FCSTD DOCUMENT  (FreeCAD 0.18R13588 (Git))
Label: footprint-Edge-template
License: All rights reserved
LicenseURL: http://en.wikipedia.org/wiki/All_rights_reserved
objects: Sketcher::SketchObject×4, App::Annotation×2, App::DocumentObjectGroup×1
note: 4 computed .brp shape members not serialized (recipe doc carries the construction recipe); baked Part::Feature solids carry a one-line shape summary decoded from their .brp

FEATURE [Sketcher::SketchObject] Sketch004  label="F_Fab_0.1"
  sketch-geometry (4):
    g0: Circle CenterX=0.0195 CenterY=-0.011 CenterZ=0 NormalX=0 NormalY=0 NormalZ=1 AngleXU=0 Radius=3.1
    g1: Circle CenterX=0.0195 CenterY=-49.011 CenterZ=0 NormalX=0 NormalY=0 NormalZ=1 AngleXU=0 Radius=3.1
    g2: Circle CenterX=58.0195 CenterY=-0.011 CenterZ=0 NormalX=0 NormalY=0 NormalZ=1 AngleXU=0 Radius=3.1
    g3: Circle CenterX=58.0195 CenterY=-49.011 CenterZ=0 NormalX=0 NormalY=0 NormalZ=1 AngleXU=0 Radius=3.1
  constraints (4):
    c: Radius(g0) = 3.1
    c: Radius(g2) = 3.1
    c: Radius(g3) = 3.1
    c: Radius(g1) = 3.1
FEATURE [Sketcher::SketchObject] Sketch  label="Edge_Cuts_0.15"
  sketch-geometry (20):
    g0: LineSegment StartX=-0.4805 StartY=3.739 StartZ=0 EndX=58.5195 EndY=3.739 EndZ=0
    g1: ArcOfCircle CenterX=-0.4805 CenterY=0.739 CenterZ=0 NormalX=0 NormalY=0 NormalZ=1 AngleXU=1.5708 Radius=3 StartAngle=0 EndAngle=1.5708
    g2: ArcOfCircle CenterX=58.5195 CenterY=0.739 CenterZ=0 NormalX=0 NormalY=0 NormalZ=1 AngleXU=0 Radius=3 StartAngle=0 EndAngle=1.5708
    g3: LineSegment StartX=-3.4805 StartY=0.739 StartZ=0 EndX=-3.4805 EndY=-15.261 EndZ=0
    g4: LineSegment StartX=61.5195 StartY=0.739 StartZ=0 EndX=61.5195 EndY=-49.761 EndZ=0
    g5: ArcOfCircle CenterX=-2.4805 CenterY=-15.261 CenterZ=0 NormalX=0 NormalY=0 NormalZ=1 AngleXU=-3.14159 Radius=1 StartAngle=0 EndAngle=1.5708
    g6: ArcOfCircle CenterX=58.5195 CenterY=-49.761 CenterZ=0 NormalX=0 NormalY=0 NormalZ=1 AngleXU=-1.5708 Radius=3 StartAngle=0 EndAngle=1.5708
    g7: LineSegment StartX=-2.4805 StartY=-16.261 StartZ=0 EndX=0.5195 EndY=-16.261 EndZ=0
    g8: LineSegment StartX=-0.4805 StartY=-52.761 StartZ=0 EndX=58.5195 EndY=-52.761 EndZ=0
    g9: ArcOfCircle CenterX=0.5195 CenterY=-17.261 CenterZ=0 NormalX=0 NormalY=0 NormalZ=1 AngleXU=0 Radius=1 StartAngle=0 EndAngle=1.5708
    g10: ArcOfCircle CenterX=-0.4805 CenterY=-49.761 CenterZ=0 NormalX=0 NormalY=0 NormalZ=1 AngleXU=3.14159 Radius=3 StartAngle=0 EndAngle=1.5708
    g11: LineSegment StartX=1.5195 StartY=-17.261 StartZ=0 EndX=1.5195 EndY=-32.261 EndZ=0
    g12: LineSegment StartX=-3.4805 StartY=-34.261 StartZ=0 EndX=-3.4805 EndY=-49.761 EndZ=0
    g13: ArcOfCircle CenterX=0.5195 CenterY=-32.261 CenterZ=0 NormalX=0 NormalY=0 NormalZ=1 AngleXU=-1.5708 Radius=1 StartAngle=0 EndAngle=1.5708
    g14: ArcOfCircle CenterX=-2.4805 CenterY=-34.261 CenterZ=0 NormalX=0 NormalY=0 NormalZ=1 AngleXU=1.5708 Radius=1 StartAngle=0 EndAngle=1.5708
    g15: LineSegment StartX=-2.4805 StartY=-33.261 StartZ=0 EndX=0.5195 EndY=-33.261 EndZ=0
    g16: LineSegment StartX=42.5195 StartY=-33.761 StartZ=0 EndX=42.5195 EndY=-48.761 EndZ=0
    g17: ArcOfCircle CenterX=41.5195 CenterY=-33.761 CenterZ=0 NormalX=0 NormalY=0 NormalZ=1 AngleXU=0 Radius=1 StartAngle=0 EndAngle=3.14159
    g18: ArcOfCircle CenterX=41.5195 CenterY=-48.761 CenterZ=0 NormalX=0 NormalY=0 NormalZ=1 AngleXU=3.14159 Radius=1 StartAngle=0 EndAngle=3.14159
    g19: LineSegment StartX=40.5195 StartY=-33.761 StartZ=0 EndX=40.5195 EndY=-48.761 EndZ=0
FEATURE [App::Annotation] Text  label="Ref#_1.0mm"
  LabelText = REF**
  Position = (1,-7,0)
FEATURE [App::Annotation] Text001  label="Value#_1.0mm"
  LabelText = Value 
  Position = (1,-10,0)
FEATURE [Sketcher::SketchObject] Sketch006  label="Pads_TH_SMD"
  sketch-geometry (83):
    g0: LineSegment StartX=4 StartY=-0.411 StartZ=0 EndX=5.76617 EndY=-0.411 EndZ=0
    g1: LineSegment StartX=5.76617 StartY=-0.411 StartZ=0 EndX=5.76617 EndY=-2.151 EndZ=0
    g2: LineSegment StartX=5.76617 StartY=-2.151 StartZ=0 EndX=4 EndY=-2.151 EndZ=0
    g3: LineSegment StartX=4 StartY=-2.151 StartZ=0 EndX=4 EndY=-0.411 EndZ=0
    g4: Circle CenterX=4.889 CenterY=1.259 CenterZ=0 NormalX=0 NormalY=0 NormalZ=1 AngleXU=0 Radius=0.87
    g5: Circle CenterX=7.429 CenterY=-1.281 CenterZ=0 NormalX=0 NormalY=0 NormalZ=1 AngleXU=0 Radius=0.87
    g6: Circle CenterX=7.429 CenterY=1.259 CenterZ=0 NormalX=0 NormalY=0 NormalZ=1 AngleXU=0 Radius=0.87
    g7: Circle CenterX=9.969 CenterY=-1.281 CenterZ=0 NormalX=0 NormalY=0 NormalZ=1 AngleXU=0 Radius=0.87
    g8: Circle CenterX=9.969 CenterY=1.259 CenterZ=0 NormalX=0 NormalY=0 NormalZ=1 AngleXU=0 Radius=0.87
    g9: Circle CenterX=12.509 CenterY=-1.281 CenterZ=0 NormalX=0 NormalY=0 NormalZ=1 AngleXU=0 Radius=0.87
    g10: Circle CenterX=12.509 CenterY=1.259 CenterZ=0 NormalX=0 NormalY=0 NormalZ=1 AngleXU=0 Radius=0.87
    g11: Circle CenterX=15.049 CenterY=-1.281 CenterZ=0 NormalX=0 NormalY=0 NormalZ=1 AngleXU=0 Radius=0.87
    g12: Circle CenterX=15.049 CenterY=1.259 CenterZ=0 NormalX=0 NormalY=0 NormalZ=1 AngleXU=0 Radius=0.87
    g13: Circle CenterX=17.589 CenterY=-1.281 CenterZ=0 NormalX=0 NormalY=0 NormalZ=1 AngleXU=0 Radius=0.87
    g14: Circle CenterX=17.589 CenterY=1.259 CenterZ=0 NormalX=0 NormalY=0 NormalZ=1 AngleXU=0 Radius=0.87
    g15: Circle CenterX=20.129 CenterY=-1.281 CenterZ=0 NormalX=0 NormalY=0 NormalZ=1 AngleXU=0 Radius=0.87
    g16: Circle CenterX=20.129 CenterY=1.259 CenterZ=0 NormalX=0 NormalY=0 NormalZ=1 AngleXU=0 Radius=0.87
    g17: Circle CenterX=22.669 CenterY=-1.281 CenterZ=0 NormalX=0 NormalY=0 NormalZ=1 AngleXU=0 Radius=0.87
    g18: Circle CenterX=22.669 CenterY=1.259 CenterZ=0 NormalX=0 NormalY=0 NormalZ=1 AngleXU=0 Radius=0.87
    g19: Circle CenterX=25.209 CenterY=-1.281 CenterZ=0 NormalX=0 NormalY=0 NormalZ=1 AngleXU=0 Radius=0.87
    g20: Circle CenterX=25.209 CenterY=1.259 CenterZ=0 NormalX=0 NormalY=0 NormalZ=1 AngleXU=0 Radius=0.87
    g21: Circle CenterX=27.749 CenterY=-1.281 CenterZ=0 NormalX=0 NormalY=0 NormalZ=1 AngleXU=0 Radius=0.87
    g22: Circle CenterX=27.749 CenterY=1.259 CenterZ=0 NormalX=0 NormalY=0 NormalZ=1 AngleXU=0 Radius=0.87
    g23: Circle CenterX=30.289 CenterY=-1.281 CenterZ=0 NormalX=0 NormalY=0 NormalZ=1 AngleXU=0 Radius=0.87
    g24: Circle CenterX=30.289 CenterY=1.259 CenterZ=0 NormalX=0 NormalY=0 NormalZ=1 AngleXU=0 Radius=0.87
    g25: Circle CenterX=32.829 CenterY=-1.281 CenterZ=0 NormalX=0 NormalY=0 NormalZ=1 AngleXU=0 Radius=0.87
    g26: Circle CenterX=32.829 CenterY=1.259 CenterZ=0 NormalX=0 NormalY=0 NormalZ=1 AngleXU=0 Radius=0.87
    g27: Circle CenterX=35.369 CenterY=-1.281 CenterZ=0 NormalX=0 NormalY=0 NormalZ=1 AngleXU=0 Radius=0.87
    g28: Circle CenterX=35.369 CenterY=1.259 CenterZ=0 NormalX=0 NormalY=0 NormalZ=1 AngleXU=0 Radius=0.87
    g29: Circle CenterX=37.909 CenterY=-1.281 CenterZ=0 NormalX=0 NormalY=0 NormalZ=1 AngleXU=0 Radius=0.87
    g30: Circle CenterX=37.909 CenterY=1.259 CenterZ=0 NormalX=0 NormalY=0 NormalZ=1 AngleXU=0 Radius=0.87
    g31: Circle CenterX=40.449 CenterY=-1.281 CenterZ=0 NormalX=0 NormalY=0 NormalZ=1 AngleXU=0 Radius=0.87
    g32: Circle CenterX=40.449 CenterY=1.259 CenterZ=0 NormalX=0 NormalY=0 NormalZ=1 AngleXU=0 Radius=0.87
    g33: Circle CenterX=42.989 CenterY=-1.281 CenterZ=0 NormalX=0 NormalY=0 NormalZ=1 AngleXU=0 Radius=0.87
    g34: Circle CenterX=42.989 CenterY=1.259 CenterZ=0 NormalX=0 NormalY=0 NormalZ=1 AngleXU=0 Radius=0.87
    g35: Circle CenterX=45.529 CenterY=-1.281 CenterZ=0 NormalX=0 NormalY=0 NormalZ=1 AngleXU=0 Radius=0.87
    g36: Circle CenterX=45.529 CenterY=1.259 CenterZ=0 NormalX=0 NormalY=0 NormalZ=1 AngleXU=0 Radius=0.87
    g37: Circle CenterX=48.069 CenterY=-1.281 CenterZ=0 NormalX=0 NormalY=0 NormalZ=1 AngleXU=0 Radius=0.87
    g38: Circle CenterX=48.069 CenterY=1.259 CenterZ=0 NormalX=0 NormalY=0 NormalZ=1 AngleXU=0 Radius=0.87
    g39: Circle CenterX=50.609 CenterY=-1.281 CenterZ=0 NormalX=0 NormalY=0 NormalZ=1 AngleXU=0 Radius=0.87
    g40: Circle CenterX=50.609 CenterY=1.259 CenterZ=0 NormalX=0 NormalY=0 NormalZ=1 AngleXU=0 Radius=0.87
    g41: Circle CenterX=53.149 CenterY=-1.281 CenterZ=0 NormalX=0 NormalY=0 NormalZ=1 AngleXU=0 Radius=0.87
    g42: Circle CenterX=53.149 CenterY=1.259 CenterZ=0 NormalX=0 NormalY=0 NormalZ=1 AngleXU=0 Radius=0.87
    g43: Circle CenterX=22.6695 CenterY=-1.281 CenterZ=0 NormalX=0 NormalY=0 NormalZ=1 AngleXU=0 Radius=0.508
    g44: Circle CenterX=25.2095 CenterY=-1.281 CenterZ=0 NormalX=0 NormalY=0 NormalZ=1 AngleXU=0 Radius=0.508
    g45: Circle CenterX=25.2095 CenterY=1.259 CenterZ=0 NormalX=0 NormalY=0 NormalZ=1 AngleXU=0 Radius=0.508
    g46: Circle CenterX=22.6695 CenterY=1.259 CenterZ=0 NormalX=0 NormalY=0 NormalZ=1 AngleXU=0 Radius=0.508
    g47: Circle CenterX=20.1295 CenterY=1.259 CenterZ=0 NormalX=0 NormalY=0 NormalZ=1 AngleXU=0 Radius=0.508
    g48: Circle CenterX=20.1295 CenterY=-1.281 CenterZ=0 NormalX=0 NormalY=0 NormalZ=1 AngleXU=0 Radius=0.508
    g49: Circle CenterX=9.9695 CenterY=-1.281 CenterZ=0 NormalX=0 NormalY=0 NormalZ=1 AngleXU=0 Radius=0.508
    g50: Circle CenterX=12.5095 CenterY=-1.281 CenterZ=0 NormalX=0 NormalY=0 NormalZ=1 AngleXU=0 Radius=0.508
    g51: Circle CenterX=9.9695 CenterY=1.259 CenterZ=0 NormalX=0 NormalY=0 NormalZ=1 AngleXU=0 Radius=0.508
    g52: Circle CenterX=15.0495 CenterY=1.259 CenterZ=0 NormalX=0 NormalY=0 NormalZ=1 AngleXU=0 Radius=0.508
    g53: Circle CenterX=12.5095 CenterY=1.259 CenterZ=0 NormalX=0 NormalY=0 NormalZ=1 AngleXU=0 Radius=0.508
    g54: Circle CenterX=15.0495 CenterY=-1.281 CenterZ=0 NormalX=0 NormalY=0 NormalZ=1 AngleXU=0 Radius=0.508
    g55: Circle CenterX=17.5895 CenterY=-1.281 CenterZ=0 NormalX=0 NormalY=0 NormalZ=1 AngleXU=0 Radius=0.508
    g56: Circle CenterX=17.5895 CenterY=1.259 CenterZ=0 NormalX=0 NormalY=0 NormalZ=1 AngleXU=0 Radius=0.508
    g57: Circle CenterX=7.4295 CenterY=-1.281 CenterZ=0 NormalX=0 NormalY=0 NormalZ=1 AngleXU=0 Radius=0.508
    g58: Circle CenterX=7.4295 CenterY=1.259 CenterZ=0 NormalX=0 NormalY=0 NormalZ=1 AngleXU=0 Radius=0.508
    g59: Circle CenterX=4.8895 CenterY=-1.281 CenterZ=0 NormalX=0 NormalY=0 NormalZ=1 AngleXU=0 Radius=0.508
    g60: Circle CenterX=4.8895 CenterY=1.259 CenterZ=0 NormalX=0 NormalY=0 NormalZ=1 AngleXU=0 Radius=0.508
    g61: Circle CenterX=53.1495 CenterY=-1.281 CenterZ=0 NormalX=0 NormalY=0 NormalZ=1 AngleXU=0 Radius=0.508
    g62: Circle CenterX=48.0695 CenterY=-1.281 CenterZ=0 NormalX=0 NormalY=0 NormalZ=1 AngleXU=0 Radius=0.508
    g63: Circle CenterX=50.6095 CenterY=-1.281 CenterZ=0 NormalX=0 NormalY=0 NormalZ=1 AngleXU=0 Radius=0.508
    g64: Circle CenterX=40.4495 CenterY=-1.281 CenterZ=0 NormalX=0 NormalY=0 NormalZ=1 AngleXU=0 Radius=0.508
    g65: Circle CenterX=42.9895 CenterY=-1.281 CenterZ=0 NormalX=0 NormalY=0 NormalZ=1 AngleXU=0 Radius=0.508
    g66: Circle CenterX=45.5295 CenterY=-1.281 CenterZ=0 NormalX=0 NormalY=0 NormalZ=1 AngleXU=0 Radius=0.508
    g67: Circle CenterX=53.1495 CenterY=1.259 CenterZ=0 NormalX=0 NormalY=0 NormalZ=1 AngleXU=0 Radius=0.508
    g68: Circle CenterX=50.6095 CenterY=1.259 CenterZ=0 NormalX=0 NormalY=0 NormalZ=1 AngleXU=0 Radius=0.508
    g69: Circle CenterX=48.0695 CenterY=1.259 CenterZ=0 NormalX=0 NormalY=0 NormalZ=1 AngleXU=0 Radius=0.508
    g70: Circle CenterX=42.9895 CenterY=1.259 CenterZ=0 NormalX=0 NormalY=0 NormalZ=1 AngleXU=0 Radius=0.508
    g71: Circle CenterX=45.5295 CenterY=1.259 CenterZ=0 NormalX=0 NormalY=0 NormalZ=1 AngleXU=0 Radius=0.508
    g72: Circle CenterX=40.4495 CenterY=1.259 CenterZ=0 NormalX=0 NormalY=0 NormalZ=1 AngleXU=0 Radius=0.508
    g73: Circle CenterX=27.7495 CenterY=1.259 CenterZ=0 NormalX=0 NormalY=0 NormalZ=1 AngleXU=0 Radius=0.508
    g74: Circle CenterX=30.2895 CenterY=1.259 CenterZ=0 NormalX=0 NormalY=0 NormalZ=1 AngleXU=0 Radius=0.508
    g75: Circle CenterX=35.3695 CenterY=1.259 CenterZ=0 NormalX=0 NormalY=0 NormalZ=1 AngleXU=0 Radius=0.508
    g76: Circle CenterX=32.8295 CenterY=1.259 CenterZ=0 NormalX=0 NormalY=0 NormalZ=1 AngleXU=0 Radius=0.508
    g77: Circle CenterX=27.7495 CenterY=-1.281 CenterZ=0 NormalX=0 NormalY=0 NormalZ=1 AngleXU=0 Radius=0.508
    g78: Circle CenterX=30.2895 CenterY=-1.281 CenterZ=0 NormalX=0 NormalY=0 NormalZ=1 AngleXU=0 Radius=0.508
    g79: Circle CenterX=32.8295 CenterY=-1.281 CenterZ=0 NormalX=0 NormalY=0 NormalZ=1 AngleXU=0 Radius=0.508
    g80: Circle CenterX=35.3695 CenterY=-1.281 CenterZ=0 NormalX=0 NormalY=0 NormalZ=1 AngleXU=0 Radius=0.508
    g81: Circle CenterX=37.9095 CenterY=-1.281 CenterZ=0 NormalX=0 NormalY=0 NormalZ=1 AngleXU=0 Radius=0.508
    g82: Circle CenterX=37.9095 CenterY=1.259 CenterZ=0 NormalX=0 NormalY=0 NormalZ=1 AngleXU=0 Radius=0.508
FEATURE [Sketcher::SketchObject] Sketch007  label="Pads_NPTH"
  sketch-geometry (8):
    g0: Circle CenterX=0.0195 CenterY=-0.011 CenterZ=0 NormalX=0 NormalY=0 NormalZ=1 AngleXU=0 Radius=1.375
    g1: Circle CenterX=0.0195 CenterY=-49.011 CenterZ=0 NormalX=0 NormalY=0 NormalZ=1 AngleXU=0 Radius=1.375
    g2: Circle CenterX=58.0195 CenterY=-0.011 CenterZ=0 NormalX=0 NormalY=0 NormalZ=1 AngleXU=0 Radius=1.375
    g3: Circle CenterX=58.0195 CenterY=-49.011 CenterZ=0 NormalX=0 NormalY=0 NormalZ=1 AngleXU=0 Radius=1.375
    g4: Circle CenterX=0.0195 CenterY=-0.011 CenterZ=0 NormalX=0 NormalY=0 NormalZ=1 AngleXU=0 Radius=1.375
    g5: Circle CenterX=0.0195 CenterY=-49.011 CenterZ=0 NormalX=0 NormalY=0 NormalZ=1 AngleXU=0 Radius=1.375
    g6: Circle CenterX=58.0195 CenterY=-0.011 CenterZ=0 NormalX=0 NormalY=0 NormalZ=1 AngleXU=0 Radius=1.375
    g7: Circle CenterX=58.0195 CenterY=-49.011 CenterZ=0 NormalX=0 NormalY=0 NormalZ=1 AngleXU=0 Radius=1.375
FEATURE [App::DocumentObjectGroup] Group  label="footprint_Edge_template"
  Group = -> [Sketch,Sketch004,Sketch006,Sketch007,Text,Text001]
